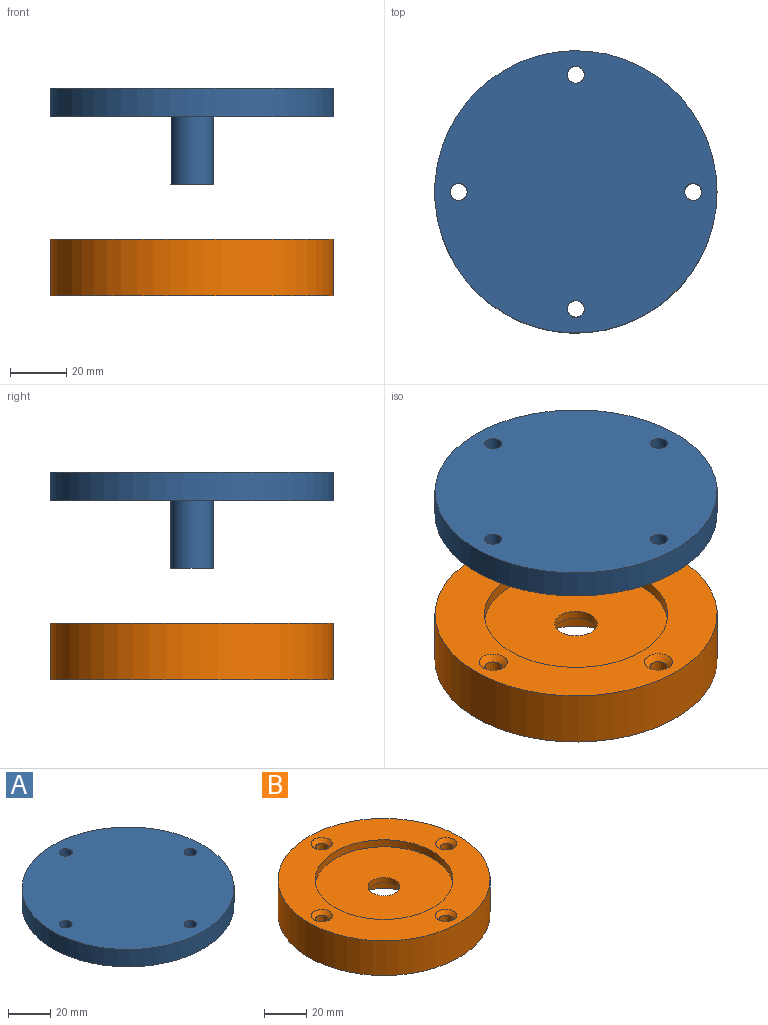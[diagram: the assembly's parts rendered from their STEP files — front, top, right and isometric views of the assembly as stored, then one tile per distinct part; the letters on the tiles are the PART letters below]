
ASSEMBLY  parts=2 mates=1
PART A: 15 faces, bbox 100x100x34 mm
  f0: cylinder r=50mm len=100mm, axis (0,0,-1), area 3141.6mm2, adj f1,f2
  f1: plane 100x100mm, normal (0,0,1), area 7740.9mm2, adj f0,f7,f9,f11,f13
  f2: plane 100x100mm, normal (0,0,-1), area 4221.5mm2, adj f0,f3,f8,f10,f12,f14
  f3: cylinder r=32.5mm len=65mm, axis (0,0,1), area 816.8mm2, adj f2,f4
  f4: plane 65x65mm, normal (0,0,-1), area 3141.6mm2, adj f3,f5
  f5: cylinder r=7.5mm len=28mm, axis (0,0,1), area 1319.5mm2, adj f4,f6
  f6: plane 15x15mm, normal (0,0,-1), area 176.7mm2, adj f5
  f7: cylinder r=3mm len=8mm, axis (0,0,-1), area 150.8mm2, adj f1,f8
  f8: cone r=3mm half-angle=45deg, axis (0,0,-1), area 71.1mm2, adj f2,f7
  f9: cylinder r=3mm len=8mm, axis (0,0,-1), area 150.8mm2, adj f1,f10
  f10: cone r=3mm half-angle=45deg, axis (0,0,-1), area 71.1mm2, adj f2,f9
  f11: cylinder r=3mm len=8mm, axis (0,0,-1), area 150.8mm2, adj f1,f12
  f12: cone r=3mm half-angle=45deg, axis (0,0,-1), area 71.1mm2, adj f2,f11
  f13: cylinder r=3mm len=8mm, axis (0,0,-1), area 150.8mm2, adj f1,f14
  f14: cone r=3mm half-angle=45deg, axis (0,0,-1), area 71.1mm2, adj f2,f13
PART B: 16 faces, bbox 100x100x20 mm
  f0: cylinder r=7.5mm len=15mm, axis (0,0,1), area 141.4mm2, adj f5,f15
  f1: cylinder r=50mm len=100mm, axis (0,0,1), area 6283.2mm2, adj f2,f3
  f2: plane 100x100mm, normal (0,0,-1), area 6355.4mm2, adj f1,f6,f8,f10,f12,f14
  f3: plane 100x100mm, normal (0,0,1), area 4221.5mm2, adj f1,f4,f7,f9,f11,f13
  f4: cylinder r=32.5mm len=65mm, axis (0,0,-1), area 816.8mm2, adj f3,f5
  f5: plane 65x65mm, normal (0,0,1), area 3141.6mm2, adj f0,f4
  f6: cylinder r=3mm len=18mm, axis (0,0,1), area 339.3mm2, adj f2,f7
  f7: cone r=3mm half-angle=45deg, axis (0,0,1), area 71.1mm2, adj f3,f6
  f8: cylinder r=3mm len=18mm, axis (0,0,1), area 339.3mm2, adj f2,f9
  f9: cone r=3mm half-angle=45deg, axis (0,0,1), area 71.1mm2, adj f3,f8
  f10: cylinder r=3mm len=18mm, axis (0,0,1), area 339.3mm2, adj f2,f11
  f11: cone r=3mm half-angle=45deg, axis (0,0,1), area 71.1mm2, adj f3,f10
  f12: cylinder r=3mm len=18mm, axis (0,0,1), area 339.3mm2, adj f2,f13
  f13: cone r=3mm half-angle=45deg, axis (0,0,1), area 71.1mm2, adj f3,f12
  f14: cylinder r=21mm len=42mm, axis (0,0,-1), area 1715.3mm2, adj f2,f15
  f15: plane 42x42mm, normal (0,0,-1), area 1208.7mm2, adj f0,f14
PLACE A t=(32.13,-48.18,96.37)mm
PLACE B t=(32.13,-48.18,76.99)mm
MATE slider B.f0 <-> A.f0  axis (0,0,-1) through (32.13,-48.18,45.99)mm
